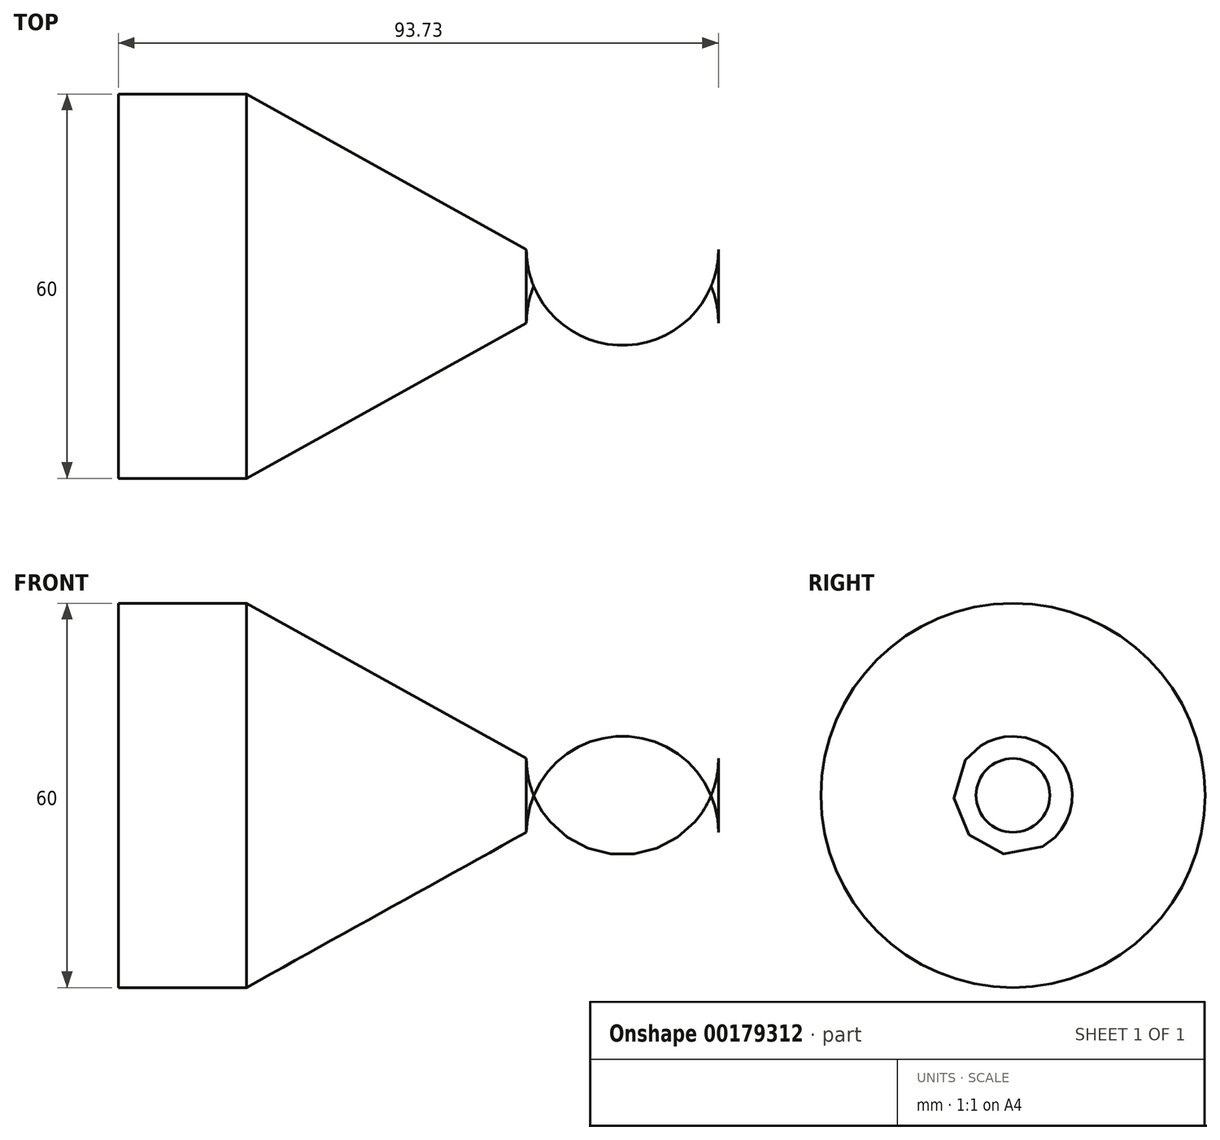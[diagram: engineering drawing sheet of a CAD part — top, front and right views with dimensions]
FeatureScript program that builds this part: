
annotation { "Feature Type Name" : "Feature", "Feature Type Description" : "" }
export const myFeature = defineFeature(function(context is Context, id is Id, definition is map)
    precondition{}
    {
        {
            var Q0;
            Q0=qCreatedBy(makeId("Front.planeOp"),FACE);
            var sketch = newSketch(context, id + "F0", { "sketchPlane" : qUnion([Q0])});
            skLineSegment(sketch, "E0", {"start": v(0, 0) * mm, "end": v(0, 30) * mm});
            skLineSegment(sketch, "E1", {"start": v(0, 30) * mm, "end": v(20, 30) * mm});
            skLineSegment(sketch, "E2", {"start": v(20, 30) * mm, "end": v(63.73, 5.76) * mm});
            skArc(sketch, "E3", {"start": v(93.73, 5.76) * mm, "mid": v(78.73, 20.76) * mm, "end": v(63.73, 5.76) * mm});
            skLineSegment(sketch, "E4", {"start": v(93.73, 5.76) * mm, "end": v(93.73, 0) * mm});
            skLineSegment(sketch, "E5", {"start": v(93.73, 0) * mm, "end": v(0, 0) * mm});
            skSolve(sketch);
        }
        {
            var Q0;
            Q0=makeQuery(id+"F0.imprint","IMPRINT",FACE,{"disambiguationData":[TD([[makeQuery(id+"F0.imprint","IMPRINT",EDGE,{"derivedFrom":sQuery(id+"F0.wireOp",EDGE,"E0")}),-1.0]])]});
            var Q1;
            Q1=sQuery(id+"F0.wireOp",EDGE,"E5");
            revolve(context, id + "F1", {"entities" : qUnion([Q0]), "axis" : qUnion([Q1]), "revolveType" : RevolveType.FULL});
        }
    });
